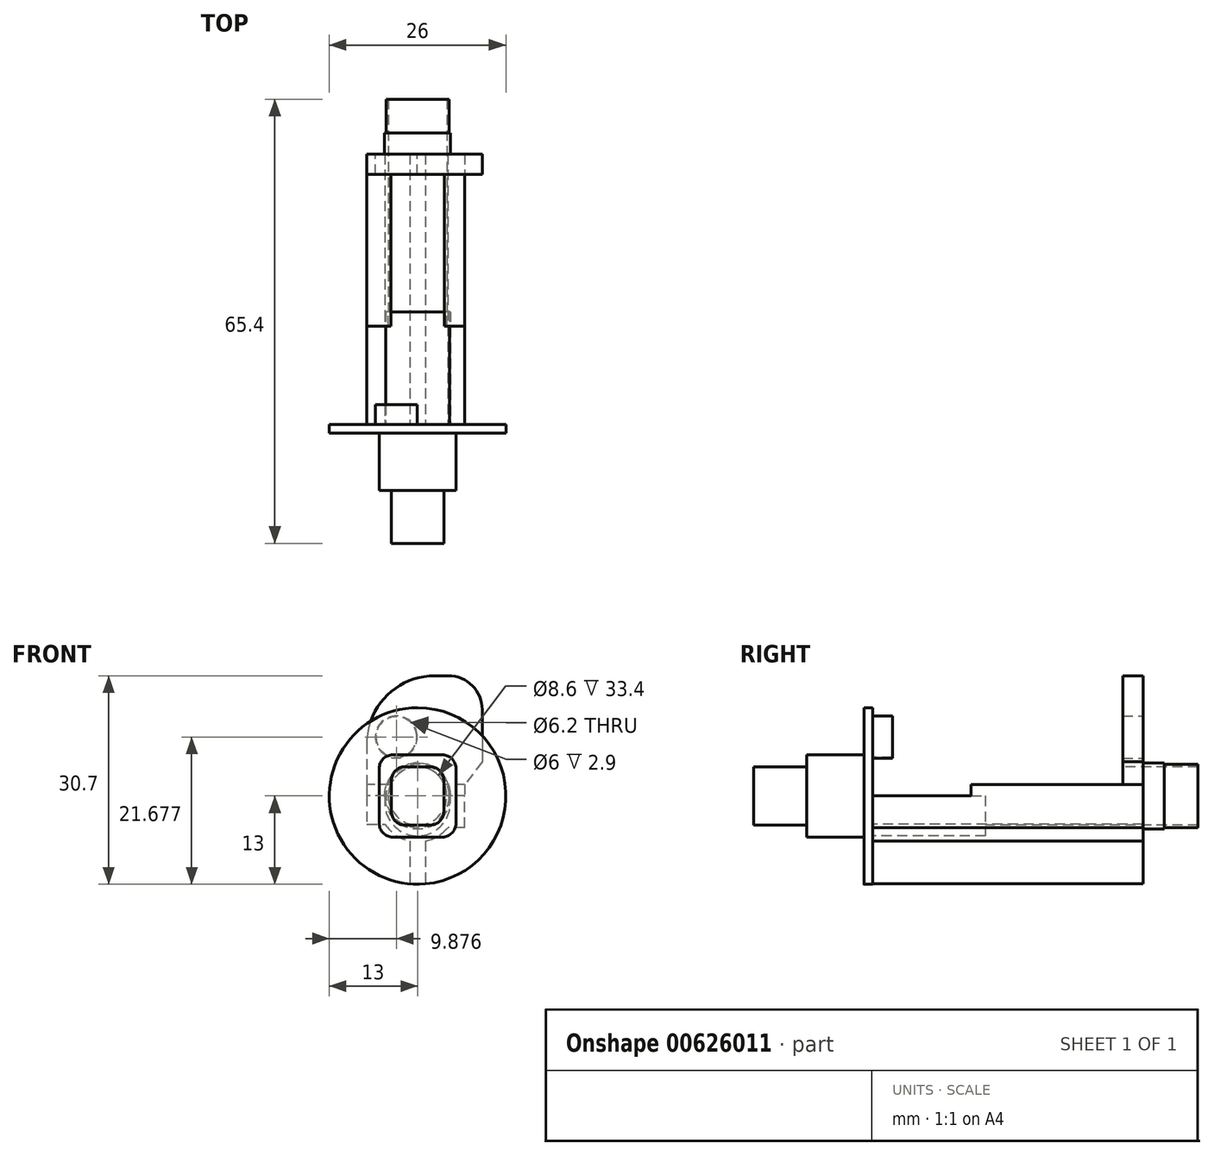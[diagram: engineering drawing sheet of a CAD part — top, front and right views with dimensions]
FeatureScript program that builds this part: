
annotation { "Feature Type Name" : "Feature", "Feature Type Description" : "" }
export const myFeature = defineFeature(function(context is Context, id is Id, definition is map)
    precondition{}
    {
        {
            var Q0;
            Q0=qCreatedBy(makeId("Front.planeOp"),FACE);
            var sketch = newSketch(context, id + "F0", { "sketchPlane" : qUnion([Q0])});
            skLineSegment(sketch, "E0.bottom", {"start": v(1.85, 4.3) * mm, "end": v(-1.85, 4.3) * mm});
            skLineSegment(sketch, "E0.top", {"start": v(1.85, -4.3) * mm, "end": v(-1.85, -4.3) * mm});
            skLineSegment(sketch, "E0.left", {"start": v(3.85, 2.3) * mm, "end": v(3.85, -2.3) * mm});
            skLineSegment(sketch, "E0.right", {"start": v(-3.85, 2.3) * mm, "end": v(-3.85, -2.3) * mm});
            skPoint(sketch, "E0.middle", {"position": v(0, 0) * mm});
            skPoint(sketch, "E1.visualSharp", {"position": v(-3.85, 4.3) * mm});
            skArc(sketch, "E1.filletArc", {"start": v(-1.85, 4.3) * mm, "mid": v(-3.26, 3.71) * mm, "end": v(-3.85, 2.3) * mm});
            skPoint(sketch, "E2.visualSharp", {"position": v(3.85, 4.3) * mm});
            skArc(sketch, "E2.filletArc", {"start": v(3.85, 2.3) * mm, "mid": v(3.26, 3.71) * mm, "end": v(1.85, 4.3) * mm});
            skPoint(sketch, "E3.visualSharp", {"position": v(3.85, -4.3) * mm});
            skArc(sketch, "E3.filletArc", {"start": v(1.85, -4.3) * mm, "mid": v(3.26, -3.71) * mm, "end": v(3.85, -2.3) * mm});
            skPoint(sketch, "E4.visualSharp", {"position": v(-3.85, -4.3) * mm});
            skArc(sketch, "E4.filletArc", {"start": v(-3.85, -2.3) * mm, "mid": v(-3.26, -3.71) * mm, "end": v(-1.85, -4.3) * mm});
            skSolve(sketch);
        }
        {
            var Q0;
            Q0=makeQuery(id+"F0.imprint","IMPRINT",FACE,{"disambiguationData":[TD([[makeQuery(id+"F0.imprint","IMPRINT",EDGE,{"derivedFrom":sQuery(id+"F0.wireOp",EDGE,"E0.bottom")}),1.0]])]});
            extrude(context, id + "F1", {"entities" : qUnion([Q0]), "oppositeDirection" : true, "depth" : 7.8 * mm, "offsetDistance" : 25 * mm});
        }
        {
            var Q0;
            Q0=makeQuery(id+"F1.opExtrude","CAP_FACE",FACE,{"disambiguationData":[OSD([sQuery(id+"F0.wireOp",EDGE,"E0.bottom"),sQuery(id+"F0.wireOp",EDGE,"E0.top"),sQuery(id+"F0.wireOp",EDGE,"E0.left"),sQuery(id+"F0.wireOp",EDGE,"E0.right"),sQuery(id+"F0.wireOp",EDGE,"E1.filletArc"),sQuery(id+"F0.wireOp",EDGE,"E2.filletArc"),sQuery(id+"F0.wireOp",EDGE,"E3.filletArc"),sQuery(id+"F0.wireOp",EDGE,"E4.filletArc")])],"isStart":false});
            var sketch = newSketch(context, id + "F2", { "sketchPlane" : qUnion([Q0])});
            skLineSegment(sketch, "E5.bottom", {"start": v(-3.65, -6.05) * mm, "end": v(3.65, -6.05) * mm});
            skLineSegment(sketch, "E5.top", {"start": v(-3.65, 6.05) * mm, "end": v(3.65, 6.05) * mm});
            skLineSegment(sketch, "E5.left", {"start": v(-5.65, -4.05) * mm, "end": v(-5.65, 4.05) * mm});
            skLineSegment(sketch, "E5.right", {"start": v(5.65, -4.05) * mm, "end": v(5.65, 4.05) * mm});
            skPoint(sketch, "E5.middle", {"position": v(0, 0) * mm});
            skPoint(sketch, "E6.visualSharp", {"position": v(5.65, -6.05) * mm});
            skArc(sketch, "E6.filletArc", {"start": v(3.65, -6.05) * mm, "mid": v(5.06, -5.46) * mm, "end": v(5.65, -4.05) * mm});
            skPoint(sketch, "E7.visualSharp", {"position": v(-5.65, -6.05) * mm});
            skArc(sketch, "E7.filletArc", {"start": v(-5.65, -4.05) * mm, "mid": v(-5.06, -5.46) * mm, "end": v(-3.65, -6.05) * mm});
            skPoint(sketch, "E8.visualSharp", {"position": v(-5.65, 6.05) * mm});
            skArc(sketch, "E8.filletArc", {"start": v(-3.65, 6.05) * mm, "mid": v(-5.06, 5.46) * mm, "end": v(-5.65, 4.05) * mm});
            skPoint(sketch, "E9.visualSharp", {"position": v(5.65, 6.05) * mm});
            skArc(sketch, "E9.filletArc", {"start": v(5.65, 4.05) * mm, "mid": v(5.06, 5.46) * mm, "end": v(3.65, 6.05) * mm});
            skSolve(sketch);
        }
        {
            var Q0;
            Q0=makeQuery(id+"F2.imprint","IMPRINT",FACE,{"disambiguationData":[TD([[makeQuery(id+"F2.imprint","IMPRINT",EDGE,{"derivedFrom":makeQuery(id+"F1.opExtrude","CAP_EDGE",EDGE,{"disambiguationData":[OSD([sQuery(id+"F0.wireOp",EDGE,"E0.bottom")])],"isStart":false})}),-1.0]])]});
            var Q1;
            Q1=makeQuery(id+"F2.imprint","IMPRINT",FACE,{"disambiguationData":[TD([[makeQuery(id+"F2.imprint","IMPRINT",EDGE,{"derivedFrom":sQuery(id+"F2.wireOp",EDGE,"E5.bottom")}),1.0]])]});
            extrude(context, id + "F3", {"entities" : qUnion([Q0, Q1]), "operationType" : NewBodyOperationType.ADD, "depth" : 8.4 * mm, "offsetDistance" : 25 * mm});
        }
        {
            var Q0;
            Q0=makeQuery(id+"F3.opExtrude","CAP_FACE",FACE,{"disambiguationData":[OSD([sQuery(id+"F2.wireOp",EDGE,"E5.bottom"),sQuery(id+"F2.wireOp",EDGE,"E5.top"),sQuery(id+"F2.wireOp",EDGE,"E5.left"),sQuery(id+"F2.wireOp",EDGE,"E5.right"),sQuery(id+"F2.wireOp",EDGE,"E6.filletArc"),sQuery(id+"F2.wireOp",EDGE,"E7.filletArc"),sQuery(id+"F2.wireOp",EDGE,"E8.filletArc"),sQuery(id+"F2.wireOp",EDGE,"E9.filletArc")])],"isStart":false});
            var sketch = newSketch(context, id + "F4", { "sketchPlane" : qUnion([Q0])});
            skCircle(sketch, "E10", {"center": v(0, 0) * mm, "radius": 13 * mm});
            skSolve(sketch);
        }
        {
            var Q0;
            Q0=makeQuery(id+"F4.imprint","IMPRINT",FACE,{"disambiguationData":[TD([[makeQuery(id+"F4.imprint","IMPRINT",EDGE,{"derivedFrom":sQuery(id+"F4.wireOp",EDGE,"E10")}),1.0]])]});
            var Q1;
            Q1=makeQuery(id+"F4.imprint","IMPRINT",FACE,{"disambiguationData":[TD([[makeQuery(id+"F4.imprint","IMPRINT",EDGE,{"derivedFrom":makeQuery(id+"F3.opExtrude","CAP_EDGE",EDGE,{"disambiguationData":[OSD([sQuery(id+"F2.wireOp",EDGE,"E5.bottom")])],"isStart":false})}),1.0]])]});
            extrude(context, id + "F5", {"entities" : qUnion([Q0, Q1]), "operationType" : NewBodyOperationType.ADD, "depth" : 1.3 * mm, "offsetDistance" : 25 * mm});
        }
        {
            var Q0;
            Q0=makeQuery(id+"F5.opExtrude","CAP_FACE",FACE,{"disambiguationData":[OSD([sQuery(id+"F4.wireOp",EDGE,"E10")])],"isStart":false});
            var sketch = newSketch(context, id + "F6", { "sketchPlane" : qUnion([Q0])});
            skLineSegment(sketch, "E11.top", {"start": v(1.15, -12.95) * mm, "end": v(-1.15, -12.95) * mm});
            skLineSegment(sketch, "E11.left", {"start": v(1.15, -6.65) * mm, "end": v(1.15, -12.95) * mm});
            skLineSegment(sketch, "E11.right", {"start": v(-1.15, -6.65) * mm, "end": v(-1.15, -12.95) * mm});
            skPoint(sketch, "E11.middle", {"position": v(0, -9.8) * mm});
            skArc(sketch, "E12", {"start": v(-5.62, 0) * mm, "mid": v(0, -6.77) * mm, "end": v(5.62, 0) * mm});
            skPoint(sketch, "E13", {"position": v(5.62, 0) * mm});
            skPoint(sketch, "E14", {"position": v(-5.62, 0) * mm});
            skLineSegment(sketch, "E15", {"start": v(-5.31, 0) * mm, "end": v(-5.62, 0) * mm});
            skLineSegment(sketch, "E16", {"start": v(-5.31, 0) * mm, "end": v(-5.31, 0) * mm});
            skLineSegment(sketch, "E17", {"start": v(-5.62, 0) * mm, "end": v(-5.31, 0) * mm});
            skLineSegment(sketch, "E18", {"start": v(-5.62, 0) * mm, "end": v(-5.62, 0) * mm});
            skCircle(sketch, "E19", {"center": v(3.12, 8.68) * mm, "radius": 3.1 * mm});
            skPoint(sketch, "E19.third.point", {"position": v(0, 13) * mm});
            skLineSegment(sketch, "E20", {"start": v(5.62, 0) * mm, "end": v(7.48, 0) * mm});
            skLineSegment(sketch, "E21", {"start": v(7.48, 0) * mm, "end": v(7.48, -4.17) * mm});
            skLineSegment(sketch, "E22", {"start": v(-6.96, -4.67) * mm, "end": v(-6.96, 0) * mm});
            skLineSegment(sketch, "E23", {"start": v(-6.96, 0) * mm, "end": v(-5.31, 0) * mm});
            skLineSegment(sketch, "E24", {"start": v(7.48, -4.17) * mm, "end": v(4.8, -4.17) * mm});
            skLineSegment(sketch, "E25", {"start": v(-6.96, -4.67) * mm, "end": v(-4.42, -4.67) * mm});
            skCircle(sketch, "E26.0", {"center": v(3.12, 8.68) * mm, "radius": 3 * mm});
            skLineSegment(sketch, "E27", {"start": v(-5.31, 0) * mm, "end": v(5.62, 0) * mm});
            skArc(sketch, "E28.0", {"start": v(-4.7, 0) * mm, "mid": v(0, -5.87) * mm, "end": v(4.7, 0) * mm});
            skLineSegment(sketch, "E29", {"start": v(5.62, 0) * mm, "end": v(6.07, 7.72) * mm});
            skLineSegment(sketch, "E30", {"start": v(-5.62, 0) * mm, "end": v(0.46, 10.26) * mm});
            skSolve(sketch);
        }
        {
            var Q0;
            Q0=makeQuery(id+"F6.imprint","IMPRINT",FACE,{"disambiguationData":[TD([[makeQuery(id+"F6.imprint","IMPRINT",EDGE,{"derivedFrom":sQuery(id+"F6.wireOp",EDGE,"E19")}),1.0]])]});
            var Q1;
            {var subQ6=sQuery(id+"F6.wireOp",EDGE,"E28.0");Q1=makeQuery(id+"F6.imprint","IMPRINT",FACE,{"disambiguationData":[TD([[makeQuery(id+"F6.imprint","IMPRINT",EDGE,{"derivedFrom":subQ6}),-1.0]])]});}
            var Q2;
            {var subQ0=sQuery(id+"F6.wireOp",EDGE,"E20");Q2=makeQuery(id+"F6.imprint","IMPRINT",FACE,{"disambiguationData":[TD([[makeQuery(id+"F6.imprint","IMPRINT",EDGE,{"derivedFrom":subQ0}),-1.0]])]});}
            var Q3;
            Q3=makeQuery(id+"F6.imprint","IMPRINT",FACE,{"disambiguationData":[TD([[makeQuery(id+"F6.imprint","IMPRINT",EDGE,{"derivedFrom":sQuery(id+"F6.wireOp",EDGE,"E11.top")}),-1.0]])]});
            var Q4;
            {var subQ4=sQuery(id+"F6.wireOp",EDGE,"E22");Q4=makeQuery(id+"F6.imprint","IMPRINT",FACE,{"disambiguationData":[TD([[makeQuery(id+"F6.imprint","IMPRINT",EDGE,{"derivedFrom":subQ4}),-1.0]])]});}
            extrude(context, id + "F7", {"entities" : qUnion([Q0, Q1, Q2, Q3, Q4]), "operationType" : NewBodyOperationType.ADD, "depth" : 5.8 * mm, "offsetDistance" : 25 * mm});
        }
        {
            var Q0;
            Q0=makeQuery(id+"F7.opExtrude","CAP_FACE",FACE,{"disambiguationData":[OSD([sQuery(id+"F6.wireOp",EDGE,"E11.top"),sQuery(id+"F6.wireOp",EDGE,"E11.left"),sQuery(id+"F6.wireOp",EDGE,"E11.right"),sQuery(id+"F6.wireOp",EDGE,"E12"),sQuery(id+"F6.wireOp",EDGE,"E20"),sQuery(id+"F6.wireOp",EDGE,"E21"),sQuery(id+"F6.wireOp",EDGE,"E22"),sQuery(id+"F6.wireOp",EDGE,"E23"),sQuery(id+"F6.wireOp",EDGE,"E24"),sQuery(id+"F6.wireOp",EDGE,"E25"),sQuery(id+"F6.wireOp",EDGE,"E27"),sQuery(id+"F6.wireOp",EDGE,"E28.0")])],"isStart":false});
            extrude(context, id + "F8", {"entities" : qUnion([Q0]), "operationType" : NewBodyOperationType.ADD, "depth" : 10.8 * mm, "offsetDistance" : 25 * mm});
        }
        {
            var Q0;
            Q0=qCreatedBy(makeId("Top.planeOp"),FACE);
            var sketch = newSketch(context, id + "F9", { "sketchPlane" : qUnion([Q0])});
            skLineSegment(sketch, "E31.0", {"start": v(6.96, 34.1) * mm, "end": v(6.96, 17.5) * mm});
            skLineSegment(sketch, "E32.0", {"start": v(4.7, 34.1) * mm, "end": v(4.7, 17.5) * mm});
            skLineSegment(sketch, "E33.0", {"start": v(-4.7, 34.1) * mm, "end": v(-4.7, 17.5) * mm});
            skLineSegment(sketch, "E34.0", {"start": v(-7.48, 34.1) * mm, "end": v(-7.48, 17.5) * mm});
            skLineSegment(sketch, "E35", {"start": v(6.96, 32) * mm, "end": v(-7.48, 32) * mm});
            skLineSegment(sketch, "E36", {"start": v(-7.48, 32) * mm, "end": v(-7.48, 57.3) * mm});
            skLineSegment(sketch, "E37", {"start": v(-7.48, 57.3) * mm, "end": v(6.96, 57.3) * mm});
            skLineSegment(sketch, "E38", {"start": v(6.96, 57.3) * mm, "end": v(6.96, 32) * mm});
            skPoint(sketch, "E39", {"position": v(6.96, 34.1) * mm});
            skPoint(sketch, "E40", {"position": v(6.96, 32) * mm});
            skSolve(sketch);
        }
        {
            var Q0;
            {var subQ5=sQuery(id+"F9.wireOp",EDGE,"E37");Q0=makeQuery(id+"F9.imprint","IMPRINT",FACE,{"disambiguationData":[TD([[makeQuery(id+"F9.imprint","IMPRINT",EDGE,{"derivedFrom":subQ5}),-1.0]])]});}
            extrude(context, id + "F10", {"entities" : qUnion([Q0]), "operationType" : NewBodyOperationType.ADD, "depth" : 1.7 * mm, "offsetDistance" : 25 * mm});
        }
        {
            var Q0;
            Q0=makeQuery(id+"F8.opExtrude","CAP_FACE",FACE,{"disambiguationData":[OSD([sQuery(id+"F6.wireOp",EDGE,"E11.top"),sQuery(id+"F6.wireOp",EDGE,"E11.left"),sQuery(id+"F6.wireOp",EDGE,"E11.right"),sQuery(id+"F6.wireOp",EDGE,"E12"),sQuery(id+"F6.wireOp",EDGE,"E20"),sQuery(id+"F6.wireOp",EDGE,"E21"),sQuery(id+"F6.wireOp",EDGE,"E22"),sQuery(id+"F6.wireOp",EDGE,"E23"),sQuery(id+"F6.wireOp",EDGE,"E24"),sQuery(id+"F6.wireOp",EDGE,"E25"),sQuery(id+"F6.wireOp",EDGE,"E27"),sQuery(id+"F6.wireOp",EDGE,"E28.0")])],"isStart":false});
            var sketch = newSketch(context, id + "F11", { "sketchPlane" : qUnion([Q0])});
            skLineSegment(sketch, "E41", {"start": v(-4.7, 0) * mm, "end": v(4.7, 0) * mm});
            skSolve(sketch);
        }
        {
            var Q0;
            Q0=makeQuery(id+"F11.imprint","IMPRINT",FACE,{"disambiguationData":[TD([[makeQuery(id+"F11.imprint","IMPRINT",EDGE,{"derivedFrom":sQuery(id+"F11.wireOp",EDGE,"E41")}),-1.0]])]});
            var Q1;
            Q1=makeQuery(id+"F11.imprint","IMPRINT",FACE,{"disambiguationData":[TD([[makeQuery(id+"F11.imprint","IMPRINT",EDGE,{"derivedFrom":makeQuery(id+"F8.opExtrude","CAP_EDGE",EDGE,{"disambiguationData":[OSD([sQuery(id+"F6.wireOp",EDGE,"E11.top")])],"isStart":false})}),-1.0]])]});
            extrude(context, id + "F12", {"entities" : qUnion([Q0, Q1]), "operationType" : NewBodyOperationType.ADD, "depth" : 23.2 * mm, "offsetDistance" : 25 * mm});
        }
        {
            var Q0;
            Q0=makeQuery(id+"F10.opExtrude","CAP_FACE",FACE,{"disambiguationData":[OSD([sQuery(id+"F9.wireOp",EDGE,"E35"),sQuery(id+"F9.wireOp",EDGE,"E36"),sQuery(id+"F9.wireOp",EDGE,"E37"),sQuery(id+"F9.wireOp",EDGE,"E38")])],"isStart":false});
            var sketch = newSketch(context, id + "F13", { "sketchPlane" : qUnion([Q0])});
            skLineSegment(sketch, "E42.bottom", {"start": v(-7.48, 54.3) * mm, "end": v(9.52, 54.3) * mm});
            skLineSegment(sketch, "E42.top", {"start": v(-7.48, 57.3) * mm, "end": v(9.52, 57.3) * mm});
            skLineSegment(sketch, "E42.left", {"start": v(-7.48, 54.3) * mm, "end": v(-7.48, 57.3) * mm});
            skLineSegment(sketch, "E42.right", {"start": v(9.52, 54.3) * mm, "end": v(9.52, 57.3) * mm});
            skSolve(sketch);
        }
        {
            var Q0;
            Q0 = qSketchRegion(id + "F13", true);
            extrude(context, id + "F14", {"entities" : qUnion([Q0]), "operationType" : NewBodyOperationType.ADD, "depth" : 16 * mm, "offsetDistance" : 25 * mm});
        }
        {
            var Q0;
            Q0=makeQuery(id+"F14.opExtrude","SWEPT_FACE",FACE,{"disambiguationData":[OSD([sQuery(id+"F13.wireOp",EDGE,"E42.bottom")])]});
            var sketch = newSketch(context, id + "F15", { "sketchPlane" : qUnion([Q0])});
            skLineSegment(sketch, "E43", {"start": v(6.96, 1.7) * mm, "end": v(9.52, 5.05) * mm});
            skSolve(sketch);
        }
        {
            var Q0;
            Q0=makeQuery(id+"F14.opExtrude","CAP_EDGE",EDGE,{"disambiguationData":[OSD([sQuery(id+"F13.wireOp",EDGE,"E42.left")])],"isStart":false});
            fillet(context, id + "F16", {"entities" : qUnion([Q0]), "radius" : 10 * mm, "tangentPropagation" : true, "allowEdgeOverflow" : false});
        }
        {
            var Q0;
            Q0=makeQuery(id+"F14.opExtrude","CAP_EDGE",EDGE,{"disambiguationData":[OSD([sQuery(id+"F13.wireOp",EDGE,"E42.right")])],"isStart":false});
            fillet(context, id + "F17", {"entities" : qUnion([Q0]), "radius" : 5 * mm, "tangentPropagation" : true, "allowEdgeOverflow" : false});
        }
        {
            var Q0;
            Q0=makeQuery(id+"F15.imprint","IMPRINT",FACE,{"disambiguationData":[TD([[makeQuery(id+"F15.imprint","IMPRINT",EDGE,{"derivedFrom":sQuery(id+"F15.wireOp",EDGE,"IegaZKSh-PWoz-v3RX-uuWv-uVQ8X6qszxXv")}),1.0]])]});
            var Q1;
            {var subQ0=sQuery(id+"F15.wireOp",EDGE,"E43");Q1=makeQuery(id+"F15.imprint","IMPRINT",FACE,{"disambiguationData":[TD([[makeQuery(id+"F15.imprint","IMPRINT",EDGE,{"derivedFrom":subQ0}),-1.0]])]});}
            extrude(context, id + "F18", {"entities" : qUnion([Q0, Q1]), "operationType" : NewBodyOperationType.REMOVE, "oppositeDirection" : true, "depth" : 25 * mm, "offsetDistance" : 25 * mm});
        }
        {
            var Q0;
            Q0=makeQuery(id+"F12.opExtrude","CAP_FACE",FACE,{"disambiguationData":[OSD([sQuery(id+"F6.wireOp",EDGE,"E11.top"),sQuery(id+"F6.wireOp",EDGE,"E11.left"),sQuery(id+"F6.wireOp",EDGE,"E11.right"),sQuery(id+"F6.wireOp",EDGE,"E12"),sQuery(id+"F6.wireOp",EDGE,"E20"),sQuery(id+"F6.wireOp",EDGE,"E21"),sQuery(id+"F6.wireOp",EDGE,"E22"),sQuery(id+"F6.wireOp",EDGE,"E23"),sQuery(id+"F6.wireOp",EDGE,"E24"),sQuery(id+"F6.wireOp",EDGE,"E25"),sQuery(id+"F6.wireOp",EDGE,"E27"),sQuery(id+"F11.wireOp",EDGE,"E41")])],"isStart":false});
            var sketch = newSketch(context, id + "F19", { "sketchPlane" : qUnion([Q0])});
            skCircle(sketch, "E44", {"center": v(0, 0) * mm, "radius": 4.85 * mm});
            skSolve(sketch);
        }
        {
            var Q0;
            Q0 = qSketchRegion(id + "F19", true);
            extrude(context, id + "F20", {"entities" : qUnion([Q0]), "operationType" : NewBodyOperationType.ADD, "depth" : 3.1 * mm, "offsetDistance" : 25 * mm});
        }
        {
            var Q0;
            Q0=makeQuery(id+"F20.opExtrude","CAP_FACE",FACE,{"disambiguationData":[OSD([sQuery(id+"F19.wireOp",EDGE,"E44")])],"isStart":false});
            var sketch = newSketch(context, id + "F21", { "sketchPlane" : qUnion([Q0])});
            skCircle(sketch, "E45", {"center": v(0, 0) * mm, "radius": 4.65 * mm});
            skCircle(sketch, "E46", {"center": v(0, 0) * mm, "radius": 4.3 * mm});
            skSolve(sketch);
        }
        {
            var Q0;
            Q0=makeQuery(id+"F21.imprint","IMPRINT",FACE,{"disambiguationData":[TD([[makeQuery(id+"F21.imprint","IMPRINT",EDGE,{"derivedFrom":sQuery(id+"F21.wireOp",EDGE,"E45")}),1.0]])]});
            extrude(context, id + "F22", {"entities" : qUnion([Q0]), "operationType" : NewBodyOperationType.ADD, "depth" : 5 * mm, "offsetDistance" : 25 * mm});
        }
        {
            var Q0;
            Q0=makeQuery(id+"F22.boolean.opBoolean","SPLIT",FACE,{"disambiguationData":[TD([makeQuery(id+"F22.opExtrude","SWEPT_FACE",FACE,{"disambiguationData":[OSD([sQuery(id+"F21.wireOp",EDGE,"E46")])]})])],"derivedFrom":makeQuery(id+"F20.opExtrude","CAP_FACE",FACE,{"disambiguationData":[OSD([sQuery(id+"F19.wireOp",EDGE,"E44")])],"isStart":false})});
            extrude(context, id + "F23", {"entities" : qUnion([Q0]), "operationType" : NewBodyOperationType.REMOVE, "oppositeDirection" : true, "depth" : 29.9 * mm, "offsetDistance" : 25 * mm});
        }
        {
            var Q0;
            Q0=makeQuery(id+"F7.opExtrude","CAP_FACE",FACE,{"disambiguationData":[OSD([sQuery(id+"F6.wireOp",EDGE,"E19"),sQuery(id+"F6.wireOp",EDGE,"E26.0")])],"isStart":false});
            extrude(context, id + "F24", {"entities" : qUnion([Q0]), "operationType" : NewBodyOperationType.ADD, "depth" : 38.7 * mm, "offsetDistance" : 25 * mm});
        }
        {
            var Q0;
            Q0=makeQuery(id+"F24.boolean.opBoolean","SPLIT",FACE,{"disambiguationData":[TD([makeQuery(id+"F24.opExtrude","SWEPT_FACE",FACE,{"disambiguationData":[OSD([sQuery(id+"F6.wireOp",EDGE,"E26.0")])]})])],"derivedFrom":makeQuery(id+"F14.boolean.opBoolean","MERGE",FACE,{"derivedFrom":[makeQuery(id+"F10.opExtrude","SWEPT_FACE",FACE,{"disambiguationData":[OSD([sQuery(id+"F9.wireOp",EDGE,"E37")])]}),makeQuery(id+"F14.opExtrude","SWEPT_FACE",FACE,{"disambiguationData":[OSD([sQuery(id+"F13.wireOp",EDGE,"E42.top")])]})]})});
            var Q1;
            Q1=makeQuery(id+"F24.opExtrude","CAP_FACE",FACE,{"disambiguationData":[OSD([sQuery(id+"F6.wireOp",EDGE,"E19"),sQuery(id+"F6.wireOp",EDGE,"E26.0")])],"isStart":false});
            extrude(context, id + "F25", {"entities" : qUnion([Q0, Q1]), "operationType" : NewBodyOperationType.REMOVE, "oppositeDirection" : true, "depth" : 37.1 * mm, "offsetDistance" : 25 * mm});
        }
        {
            var Q0;
            Q0=makeQuery(id+"F25.boolean.opBoolean","COPY",FACE,{"derivedFrom":makeQuery(id+"F25.opExtrude","CAP_FACE",FACE,{"disambiguationData":[OSD([sQuery(id+"F6.wireOp",EDGE,"E19"),sQuery(id+"F6.wireOp",EDGE,"E26.0")])],"isStart":false})});
            extrude(context, id + "F26", {"entities" : qUnion([Q0]), "operationType" : NewBodyOperationType.REMOVE, "oppositeDirection" : true, "depth" : 4.5 * mm, "offsetDistance" : 25 * mm});
        }
    });
